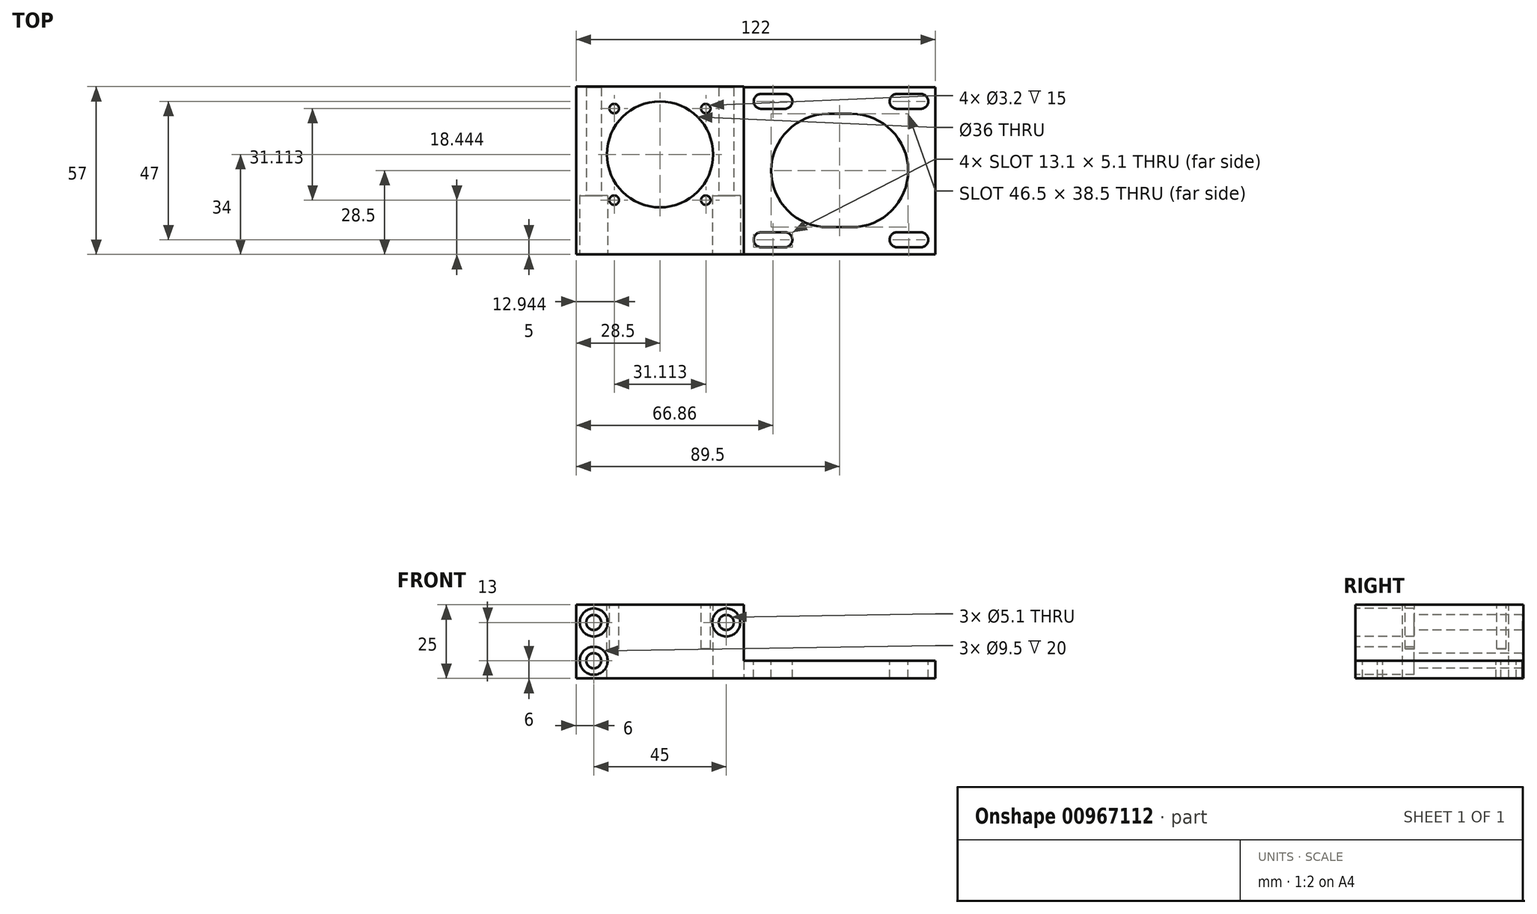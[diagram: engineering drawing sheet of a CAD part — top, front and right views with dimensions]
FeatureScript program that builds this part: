
annotation { "Feature Type Name" : "Feature", "Feature Type Description" : "" }
export const myFeature = defineFeature(function(context is Context, id is Id, definition is map)
    precondition{}
    {
        {
            var Q0;
            Q0=qCreatedBy(makeId("Top.planeOp"),FACE);
            var sketch = newSketch(context, id + "F0", { "sketchPlane" : qUnion([Q0])});
            skLineSegment(sketch, "E0.bottom", {"start": v(0, 0) * mm, "end": v(122, 0) * mm});
            skLineSegment(sketch, "E0.top", {"start": v(0, -57) * mm, "end": v(122, -57) * mm});
            skLineSegment(sketch, "E0.left", {"start": v(0, 0) * mm, "end": v(0, -57) * mm});
            skLineSegment(sketch, "E0.right", {"start": v(122, 0) * mm, "end": v(122, -57) * mm});
            skLineSegment(sketch, "E1", {"start": v(57, 0) * mm, "end": v(57, -57) * mm});
            skCircle(sketch, "E2", {"center": v(28.5, -23) * mm, "radius": 18 * mm});
            skPoint(sketch, "E3", {"position": v(93.5, -28.5) * mm});
            skCircle(sketch, "E4", {"center": v(28.5, -23) * mm, "radius": 22 * mm, "construction": true});
            skLineSegment(sketch, "E5", {"start": v(28.5, -23) * mm, "end": v(0, -23) * mm, "construction": true});
            skLineSegment(sketch, "E6", {"start": v(28.5, -23) * mm, "end": v(12.94, -7.44) * mm, "construction": true});
            skCircle(sketch, "E7", {"center": v(12.94, -7.44) * mm, "radius": 1.6 * mm});
            skCircle(sketch, "E8.1.0", {"center": v(12.94, -38.56) * mm, "radius": 1.6 * mm});
            skCircle(sketch, "E8.2.0", {"center": v(44.06, -38.56) * mm, "radius": 1.6 * mm});
            skCircle(sketch, "E8.3.0", {"center": v(44.06, -7.44) * mm, "radius": 1.6 * mm});
            skLineSegment(sketch, "E9", {"start": v(109, -5) * mm, "end": v(117, -5) * mm});
            skLineSegment(sketch, "E10", {"start": v(109, -52) * mm, "end": v(117, -52) * mm});
            skArc(sketch, "E11.0.startCap", {"start": v(109, -7.55) * mm, "mid": v(106.45, -5) * mm, "end": v(109, -2.45) * mm});
            skArc(sketch, "E11.0.endCap", {"start": v(117, -2.45) * mm, "mid": v(119.55, -5) * mm, "end": v(117, -7.55) * mm});
            skLineSegment(sketch, "E11.0.left", {"start": v(109, -2.45) * mm, "end": v(117, -2.45) * mm});
            skLineSegment(sketch, "E11.0.right", {"start": v(109, -7.55) * mm, "end": v(117, -7.55) * mm});
            skArc(sketch, "E12.0.startCap", {"start": v(109, -54.55) * mm, "mid": v(106.45, -52) * mm, "end": v(109, -49.45) * mm});
            skArc(sketch, "E12.0.endCap", {"start": v(117, -49.45) * mm, "mid": v(119.55, -52) * mm, "end": v(117, -54.55) * mm});
            skLineSegment(sketch, "E12.0.left", {"start": v(109, -49.45) * mm, "end": v(117, -49.45) * mm});
            skLineSegment(sketch, "E12.0.right", {"start": v(109, -54.55) * mm, "end": v(117, -54.55) * mm});
            skLineSegment(sketch, "E13", {"start": v(93.5, -28.5) * mm, "end": v(85.5, -28.5) * mm});
            skArc(sketch, "E14.0.startCap", {"start": v(93.5, -9.25) * mm, "mid": v(112.75, -28.5) * mm, "end": v(93.5, -47.75) * mm});
            skArc(sketch, "E14.0.endCap", {"start": v(85.5, -47.75) * mm, "mid": v(66.25, -28.5) * mm, "end": v(85.5, -9.25) * mm});
            skLineSegment(sketch, "E14.0.left", {"start": v(93.5, -47.75) * mm, "end": v(85.5, -47.75) * mm});
            skLineSegment(sketch, "E14.0.right", {"start": v(93.5, -9.25) * mm, "end": v(85.5, -9.25) * mm});
            skArc(sketch, "E15.0.startCap", {"start": v(93.5, -15) * mm, "mid": v(107, -28.5) * mm, "end": v(93.5, -42) * mm});
            skArc(sketch, "E15.0.endCap", {"start": v(85.5, -42) * mm, "mid": v(72, -28.5) * mm, "end": v(85.5, -15) * mm});
            skLineSegment(sketch, "E15.0.left", {"start": v(93.5, -42) * mm, "end": v(85.5, -42) * mm});
            skLineSegment(sketch, "E15.0.right", {"start": v(93.5, -15) * mm, "end": v(85.5, -15) * mm});
            skLineSegment(sketch, "E16", {"start": v(70.86, -5) * mm, "end": v(62.86, -5) * mm});
            skLineSegment(sketch, "E17", {"start": v(70.86, -52) * mm, "end": v(62.86, -52) * mm});
            skArc(sketch, "E18.0.startCap", {"start": v(70.86, -2.45) * mm, "mid": v(73.4, -5) * mm, "end": v(70.86, -7.55) * mm});
            skArc(sketch, "E18.0.endCap", {"start": v(62.86, -7.55) * mm, "mid": v(60.31, -5) * mm, "end": v(62.86, -2.45) * mm});
            skLineSegment(sketch, "E18.0.left", {"start": v(70.86, -7.55) * mm, "end": v(62.86, -7.55) * mm});
            skLineSegment(sketch, "E18.0.right", {"start": v(70.86, -2.45) * mm, "end": v(62.86, -2.45) * mm});
            skArc(sketch, "E19.0.startCap", {"start": v(70.86, -49.45) * mm, "mid": v(73.4, -52) * mm, "end": v(70.86, -54.55) * mm});
            skArc(sketch, "E19.0.endCap", {"start": v(62.86, -54.55) * mm, "mid": v(60.31, -52) * mm, "end": v(62.86, -49.45) * mm});
            skLineSegment(sketch, "E19.0.left", {"start": v(70.86, -54.55) * mm, "end": v(62.86, -54.55) * mm});
            skLineSegment(sketch, "E19.0.right", {"start": v(70.86, -49.45) * mm, "end": v(62.86, -49.45) * mm});
            skSolve(sketch);
        }
        {
            var Q0;
            {var subQ0=sQuery(id+"F0.wireOp",EDGE,"E0.left");Q0=makeQuery(id+"F0.imprint","IMPRINT",FACE,{"disambiguationData":[TD([[makeQuery(id+"F0.imprint","IMPRINT",EDGE,{"derivedFrom":subQ0}),1.0]])]});}
            var Q1;
            {var subQ0=sQuery(id+"F0.wireOp",EDGE,"E0.right");Q1=makeQuery(id+"F0.imprint","IMPRINT",FACE,{"disambiguationData":[TD([[makeQuery(id+"F0.imprint","IMPRINT",EDGE,{"derivedFrom":subQ0}),-1.0]])]});}
            var Q2;
            Q2=makeQuery(id+"F0.imprint","IMPRINT",FACE,{"disambiguationData":[TD([[makeQuery(id+"F0.imprint","IMPRINT",EDGE,{"derivedFrom":sQuery(id+"F0.wireOp",EDGE,"w8PoR29l-cVXJ-B1CG-RQHs-bFK6X1z3zd8K")}),-1.0]])]});
            var Q3;
            Q3=makeQuery(id+"F0.imprint","IMPRINT",FACE,{"disambiguationData":[TD([[makeQuery(id+"F0.imprint","IMPRINT",EDGE,{"derivedFrom":sQuery(id+"F0.wireOp",EDGE,"E7")}),1.0]])]});
            var Q4;
            Q4=makeQuery(id+"F0.imprint","IMPRINT",FACE,{"disambiguationData":[TD([[makeQuery(id+"F0.imprint","IMPRINT",EDGE,{"derivedFrom":sQuery(id+"F0.wireOp",EDGE,"E8.3.0")}),1.0]])]});
            var Q5;
            Q5=makeQuery(id+"F0.imprint","IMPRINT",FACE,{"disambiguationData":[TD([[makeQuery(id+"F0.imprint","IMPRINT",EDGE,{"derivedFrom":sQuery(id+"F0.wireOp",EDGE,"E8.2.0")}),1.0]])]});
            var Q6;
            Q6=makeQuery(id+"F0.imprint","IMPRINT",FACE,{"disambiguationData":[TD([[makeQuery(id+"F0.imprint","IMPRINT",EDGE,{"derivedFrom":sQuery(id+"F0.wireOp",EDGE,"E8.1.0")}),1.0]])]});
            var Q7;
            Q7=makeQuery(id+"F0.imprint","IMPRINT",FACE,{"disambiguationData":[TD([[makeQuery(id+"F0.imprint","IMPRINT",EDGE,{"derivedFrom":sQuery(id+"F0.wireOp",EDGE,"E14.0.startCap")}),-1.0]])]});
            extrude(context, id + "F1", {"entities" : qUnion([Q0, Q1, Q2, Q3, Q4, Q5, Q6, Q7]), "oppositeDirection" : true, "depth" : 25 * mm, "offsetDistance" : 25 * mm});
        }
        {
            var Q0;
            {var subQ0=sQuery(id+"F0.wireOp",EDGE,"E0.right");Q0=makeQuery(id+"F0.imprint","IMPRINT",FACE,{"disambiguationData":[TD([[makeQuery(id+"F0.imprint","IMPRINT",EDGE,{"derivedFrom":subQ0}),-1.0]])]});}
            var Q1;
            Q1=makeQuery(id+"F0.imprint","IMPRINT",FACE,{"disambiguationData":[TD([[makeQuery(id+"F0.imprint","IMPRINT",EDGE,{"derivedFrom":sQuery(id+"F0.wireOp",EDGE,"w8PoR29l-cVXJ-B1CG-RQHs-bFK6X1z3zd8K")}),-1.0]])]});
            extrude(context, id + "F2", {"entities" : qUnion([Q0, Q1]), "operationType" : NewBodyOperationType.REMOVE, "oppositeDirection" : true, "depth" : 17 * mm, "offsetDistance" : 25 * mm});
        }
        {
            var Q0;
            Q0=makeQuery(id+"F0.imprint","IMPRINT",FACE,{"disambiguationData":[TD([[makeQuery(id+"F0.imprint","IMPRINT",EDGE,{"derivedFrom":sQuery(id+"F0.wireOp",EDGE,"w8PoR29l-cVXJ-B1CG-RQHs-bFK6X1z3zd8K")}),-1.0]])]});
            var Q1;
            Q1=makeQuery(id+"F0.imprint","IMPRINT",FACE,{"disambiguationData":[TD([[makeQuery(id+"F0.imprint","IMPRINT",EDGE,{"derivedFrom":sQuery(id+"F0.wireOp",EDGE,"E14.0.startCap")}),-1.0]])]});
            var Q2;
            Q2=makeQuery(id+"F0.imprint","IMPRINT",FACE,{"disambiguationData":[TD([[makeQuery(id+"F0.imprint","IMPRINT",EDGE,{"derivedFrom":sQuery(id+"F0.wireOp",EDGE,"E15.0.startCap")}),-1.0]])]});
            extrude(context, id + "F3", {"entities" : qUnion([Q0, Q1, Q2]), "operationType" : NewBodyOperationType.REMOVE, "oppositeDirection" : true, "depth" : 19 * mm, "offsetDistance" : 25 * mm});
        }
        {
            var Q0;
            Q0=makeQuery(id+"F1.opExtrude","SWEPT_FACE",FACE,{"disambiguationData":[OSD([sQuery(id+"F0.wireOp",EDGE,"E0.top")])]});
            var sketch = newSketch(context, id + "F4", { "sketchPlane" : qUnion([Q0])});
            skCircle(sketch, "E20", {"center": v(6, -6) * mm, "radius": 4.75 * mm});
            skCircle(sketch, "E21", {"center": v(6, -6) * mm, "radius": 2.55 * mm});
            skCircle(sketch, "E22.0.1.0", {"center": v(6, -19) * mm, "radius": 2.55 * mm});
            skCircle(sketch, "E22.0.1.1", {"center": v(6, -19) * mm, "radius": 4.75 * mm});
            skCircle(sketch, "E22.1.0.0", {"center": v(51, -6) * mm, "radius": 2.55 * mm});
            skCircle(sketch, "E22.1.0.1", {"center": v(51, -6) * mm, "radius": 4.75 * mm});
            skCircle(sketch, "E22.1.1.0", {"center": v(51, -19) * mm, "radius": 2.55 * mm});
            skCircle(sketch, "E22.1.1.1", {"center": v(51, -19) * mm, "radius": 4.75 * mm});
            skCircle(sketch, "E22.2.0.0", {"center": v(96, -6) * mm, "radius": 2.55 * mm});
            skCircle(sketch, "E22.2.0.1", {"center": v(96, -6) * mm, "radius": 4.75 * mm});
            skCircle(sketch, "E22.2.1.0", {"center": v(96, -19) * mm, "radius": 2.55 * mm});
            skCircle(sketch, "E22.2.1.1", {"center": v(96, -19) * mm, "radius": 4.75 * mm});
            skLineSegment(sketch, "E22.direction1", {"start": v(6, -6) * mm, "end": v(51, -6) * mm, "construction": true});
            skLineSegment(sketch, "E22.direction2", {"start": v(6, -6) * mm, "end": v(6, -19) * mm, "construction": true});
            skSolve(sketch);
        }
        {
            var Q0;
            Q0=makeQuery(id+"F4.imprint","IMPRINT",FACE,{"disambiguationData":[TD([[makeQuery(id+"F4.imprint","IMPRINT",EDGE,{"derivedFrom":sQuery(id+"F4.wireOp",EDGE,"E21")}),1.0]])]});
            var Q1;
            Q1=makeQuery(id+"F4.imprint","IMPRINT",FACE,{"disambiguationData":[TD([[makeQuery(id+"F4.imprint","IMPRINT",EDGE,{"derivedFrom":sQuery(id+"F4.wireOp",EDGE,"E22.0.1.0")}),1.0]])]});
            var Q2;
            Q2=makeQuery(id+"F4.imprint","IMPRINT",FACE,{"disambiguationData":[TD([[makeQuery(id+"F4.imprint","IMPRINT",EDGE,{"derivedFrom":sQuery(id+"F4.wireOp",EDGE,"E22.1.0.0")}),1.0]])]});
            extrude(context, id + "F5", {"entities" : qUnion([Q0, Q1, Q2]), "operationType" : NewBodyOperationType.REMOVE, "oppositeDirection" : true, "depth" : 60 * mm, "offsetDistance" : 25 * mm});
        }
        {
            var Q0;
            Q0=makeQuery(id+"F4.imprint","IMPRINT",FACE,{"disambiguationData":[TD([[makeQuery(id+"F4.imprint","IMPRINT",EDGE,{"derivedFrom":sQuery(id+"F4.wireOp",EDGE,"E20")}),1.0]])]});
            var Q1;
            Q1=makeQuery(id+"F4.imprint","IMPRINT",FACE,{"disambiguationData":[TD([[makeQuery(id+"F4.imprint","IMPRINT",EDGE,{"derivedFrom":sQuery(id+"F4.wireOp",EDGE,"E22.0.1.0")}),-1.0]])]});
            var Q2;
            Q2=makeQuery(id+"F4.imprint","IMPRINT",FACE,{"disambiguationData":[TD([[makeQuery(id+"F4.imprint","IMPRINT",EDGE,{"derivedFrom":sQuery(id+"F4.wireOp",EDGE,"E22.1.0.0")}),-1.0]])]});
            extrude(context, id + "F6", {"entities" : qUnion([Q0, Q1, Q2]), "operationType" : NewBodyOperationType.REMOVE, "oppositeDirection" : true, "depth" : 20 * mm, "offsetDistance" : 25 * mm});
        }
        {
            var Q0;
            Q0=makeQuery(id+"F0.imprint","IMPRINT",FACE,{"disambiguationData":[TD([[makeQuery(id+"F0.imprint","IMPRINT",EDGE,{"derivedFrom":sQuery(id+"F0.wireOp",EDGE,"E8.3.0")}),1.0]])]});
            var Q1;
            Q1=makeQuery(id+"F0.imprint","IMPRINT",FACE,{"disambiguationData":[TD([[makeQuery(id+"F0.imprint","IMPRINT",EDGE,{"derivedFrom":sQuery(id+"F0.wireOp",EDGE,"E8.2.0")}),1.0]])]});
            var Q2;
            Q2=makeQuery(id+"F0.imprint","IMPRINT",FACE,{"disambiguationData":[TD([[makeQuery(id+"F0.imprint","IMPRINT",EDGE,{"derivedFrom":sQuery(id+"F0.wireOp",EDGE,"E8.1.0")}),1.0]])]});
            var Q3;
            Q3=makeQuery(id+"F0.imprint","IMPRINT",FACE,{"disambiguationData":[TD([[makeQuery(id+"F0.imprint","IMPRINT",EDGE,{"derivedFrom":sQuery(id+"F0.wireOp",EDGE,"E7")}),1.0]])]});
            extrude(context, id + "F7", {"entities" : qUnion([Q0, Q1, Q2, Q3]), "operationType" : NewBodyOperationType.REMOVE, "oppositeDirection" : true, "depth" : 15 * mm, "offsetDistance" : 25 * mm});
        }
        {
            var Q0;
            Q0=makeQuery(id+"F1.opExtrude","SWEPT_FACE",FACE,{"disambiguationData":[OSD([sQuery(id+"F0.wireOp",EDGE,"E0.bottom")])]});
            var sketch = newSketch(context, id + "F8", { "sketchPlane" : qUnion([Q0])});
            skLineSegment(sketch, "E23", {"start": v(-57, -17) * mm, "end": v(-57, -25.38) * mm});
            skSolve(sketch);
        }
        {
            var Q0;
            {var subQ0=sQuery(id+"F8.wireOp",EDGE,"E23");Q0=makeQuery(id+"F8.imprint","IMPRINT",FACE,{"disambiguationData":[TD([[makeQuery(id+"F8.imprint","IMPRINT",EDGE,{"derivedFrom":subQ0}),-1.0]])]});}
            extrude(context, id + "F9", {"entities" : qUnion([Q0]), "operationType" : NewBodyOperationType.REMOVE, "oppositeDirection" : true, "depth" : .25 * mm, "offsetDistance" : 25 * mm});
        }
        {
            var Q0;
            Q0=makeQuery(id+"F5.boolean.opBoolean","INTERSECT",EDGE,{"derivedFrom":[makeQuery(id+"F1.opExtrude","SWEPT_FACE",FACE,{"disambiguationData":[OSD([sQuery(id+"F0.wireOp",EDGE,"E0.bottom")])]}),makeQuery(id+"F5.opExtrude","SWEPT_FACE",FACE,{"disambiguationData":[OSD([sQuery(id+"F4.wireOp",EDGE,"E22.1.0.0")])]})]});
            var Q1;
            Q1=makeQuery(id+"F5.boolean.opBoolean","INTERSECT",EDGE,{"derivedFrom":[makeQuery(id+"F1.opExtrude","SWEPT_FACE",FACE,{"disambiguationData":[OSD([sQuery(id+"F0.wireOp",EDGE,"E0.bottom")])]}),makeQuery(id+"F5.opExtrude","SWEPT_FACE",FACE,{"disambiguationData":[OSD([sQuery(id+"F4.wireOp",EDGE,"E21")])]})]});
            var Q2;
            Q2=makeQuery(id+"F5.boolean.opBoolean","INTERSECT",EDGE,{"derivedFrom":[makeQuery(id+"F1.opExtrude","SWEPT_FACE",FACE,{"disambiguationData":[OSD([sQuery(id+"F0.wireOp",EDGE,"E0.bottom")])]}),makeQuery(id+"F5.opExtrude","SWEPT_FACE",FACE,{"disambiguationData":[OSD([sQuery(id+"F4.wireOp",EDGE,"E22.0.1.0")])]})]});
            chamfer(context, id + "F10", {"entities" : qUnion([Q0, Q1, Q2]), "width" : .2 * mm, "tangentPropagation" : true});
        }
    });
